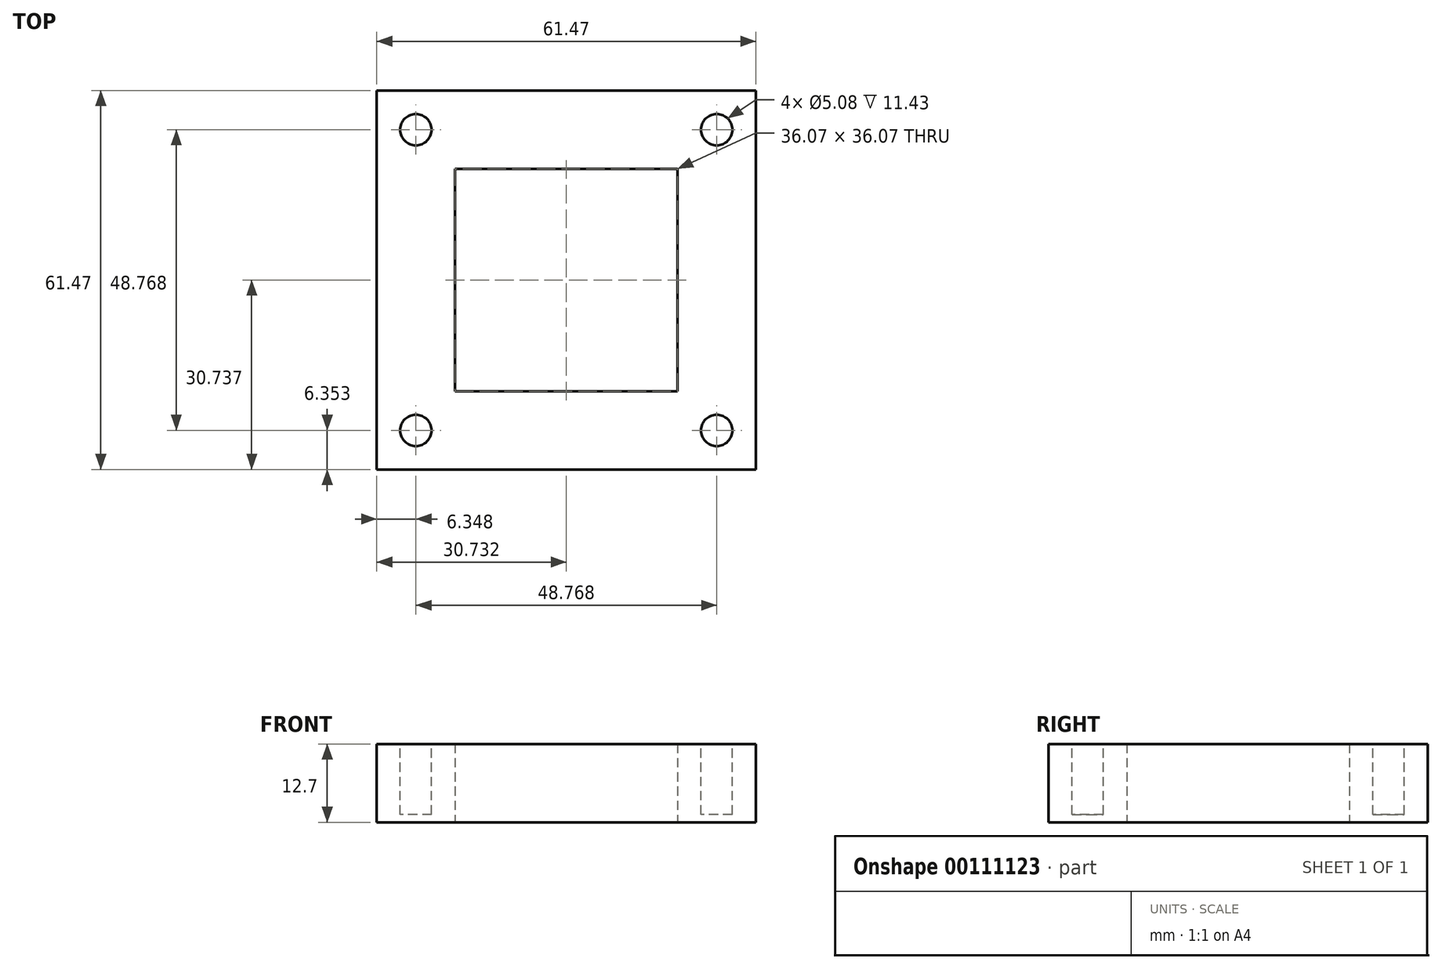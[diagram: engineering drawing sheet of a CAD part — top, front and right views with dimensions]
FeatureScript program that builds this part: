
annotation { "Feature Type Name" : "Feature", "Feature Type Description" : "" }
export const myFeature = defineFeature(function(context is Context, id is Id, definition is map)
    precondition{}
    {
        {
            var Q0;
            Q0=qCreatedBy(makeId("Top.planeOp"),FACE);
            var sketch = newSketch(context, id + "F0", { "sketchPlane" : qUnion([Q0])});
            skLineSegment(sketch, "E0.bottom", {"start": v(-23.03, 42) * mm, "end": v(38.44, 42) * mm});
            skLineSegment(sketch, "E0.top", {"start": v(-23.03, -19.47) * mm, "end": v(38.44, -19.47) * mm});
            skLineSegment(sketch, "E0.left", {"start": v(-23.03, 42) * mm, "end": v(-23.03, -19.47) * mm});
            skLineSegment(sketch, "E0.right", {"start": v(38.44, 42) * mm, "end": v(38.44, -19.47) * mm});
            skLineSegment(sketch, "E1", {"start": v(-10.33, 42) * mm, "end": v(-10.33, -19.47) * mm, "construction": true});
            skLineSegment(sketch, "E2", {"start": v(25.74, 42) * mm, "end": v(25.74, -19.47) * mm, "construction": true});
            skLineSegment(sketch, "E3", {"start": v(-23.03, 29.3) * mm, "end": v(38.44, 29.3) * mm, "construction": true});
            skLineSegment(sketch, "E4", {"start": v(-23.03, -6.77) * mm, "end": v(38.44, -6.77) * mm, "construction": true});
            skLineSegment(sketch, "E5", {"start": v(-23.03, 42) * mm, "end": v(38.44, -19.47) * mm, "construction": true});
            skLineSegment(sketch, "E6", {"start": v(-23.03, -19.47) * mm, "end": v(38.44, 42) * mm, "construction": true});
            skLineSegment(sketch, "E7", {"start": v(-23.03, 29.3) * mm, "end": v(-10.33, 42) * mm, "construction": true});
            skLineSegment(sketch, "E8", {"start": v(25.74, 42) * mm, "end": v(38.44, 29.3) * mm, "construction": true});
            skLineSegment(sketch, "E9", {"start": v(38.44, -6.77) * mm, "end": v(25.74, -19.47) * mm, "construction": true});
            skLineSegment(sketch, "E10", {"start": v(-23.03, -6.77) * mm, "end": v(-10.33, -19.47) * mm, "construction": true});
            skLineSegment(sketch, "E11.bottom", {"start": v(-10.33, 29.3) * mm, "end": v(25.74, 29.3) * mm});
            skLineSegment(sketch, "E11.top", {"start": v(-10.33, -6.77) * mm, "end": v(25.74, -6.77) * mm});
            skLineSegment(sketch, "E11.left", {"start": v(-10.33, 29.3) * mm, "end": v(-10.33, -6.77) * mm});
            skLineSegment(sketch, "E11.right", {"start": v(25.74, 29.3) * mm, "end": v(25.74, -6.77) * mm});
            skSolve(sketch);
        }
        {
            var Q0;
            Q0=makeQuery(id+"F0.imprint","IMPRINT",FACE,{"disambiguationData":[TD([[makeQuery(id+"F0.imprint","IMPRINT",EDGE,{"derivedFrom":sQuery(id+"F0.wireOp",EDGE,"E0.bottom")}),-1.0]])]});
            extrude(context, id + "F1", {"entities" : qUnion([Q0]), "depth" : 12.7 * mm});
        }
        {
            var Q0;
            Q0=makeQuery(id+"F1.opExtrude","CAP_FACE",FACE,{"disambiguationData":[OSD([sQuery(id+"F0.wireOp",EDGE,"E0.bottom"),sQuery(id+"F0.wireOp",EDGE,"E0.top"),sQuery(id+"F0.wireOp",EDGE,"E0.left"),sQuery(id+"F0.wireOp",EDGE,"E0.right"),sQuery(id+"F0.wireOp",EDGE,"E11.bottom"),sQuery(id+"F0.wireOp",EDGE,"E11.top"),sQuery(id+"F0.wireOp",EDGE,"E11.left"),sQuery(id+"F0.wireOp",EDGE,"E11.right")])],"isStart":false});
            var sketch = newSketch(context, id + "F2", { "sketchPlane" : qUnion([Q0])});
            skLineSegment(sketch, "E12", {"start": v(-10.33, 42) * mm, "end": v(-10.33, -19.47) * mm, "construction": true});
            skLineSegment(sketch, "E13", {"start": v(25.74, 42) * mm, "end": v(25.74, -19.47) * mm, "construction": true});
            skLineSegment(sketch, "E14", {"start": v(-23.03, -6.77) * mm, "end": v(38.44, -6.77) * mm, "construction": true});
            skLineSegment(sketch, "E15", {"start": v(38.44, 29.3) * mm, "end": v(-23.03, 29.3) * mm, "construction": true});
            skLineSegment(sketch, "E16", {"start": v(-23.03, 42) * mm, "end": v(38.44, -19.47) * mm, "construction": true});
            skLineSegment(sketch, "E17", {"start": v(38.44, 42) * mm, "end": v(-23.03, -19.47) * mm, "construction": true});
            skLineSegment(sketch, "E18", {"start": v(-23.03, 29.3) * mm, "end": v(-10.33, 42) * mm, "construction": true});
            skLineSegment(sketch, "E19", {"start": v(25.74, 42) * mm, "end": v(38.44, 29.3) * mm, "construction": true});
            skLineSegment(sketch, "E20", {"start": v(38.44, -6.77) * mm, "end": v(25.74, -19.47) * mm, "construction": true});
            skLineSegment(sketch, "E21", {"start": v(-23.03, -6.77) * mm, "end": v(-10.33, -19.47) * mm, "construction": true});
            skCircle(sketch, "E22", {"center": v(-16.68, 35.65) * mm, "radius": 2.54 * mm});
            skCircle(sketch, "E23", {"center": v(32.09, 35.65) * mm, "radius": 2.54 * mm});
            skCircle(sketch, "E24", {"center": v(32.09, -13.12) * mm, "radius": 2.54 * mm});
            skCircle(sketch, "E25", {"center": v(-16.68, -13.12) * mm, "radius": 2.54 * mm});
            skSolve(sketch);
        }
        {
            var Q0;
            Q0 = qSketchRegion(id + "F2", true);
            extrude(context, id + "F3", {"entities" : qUnion([Q0]), "operationType" : NewBodyOperationType.REMOVE, "oppositeDirection" : true, "depth" : 11.43 * mm});
        }
    });
